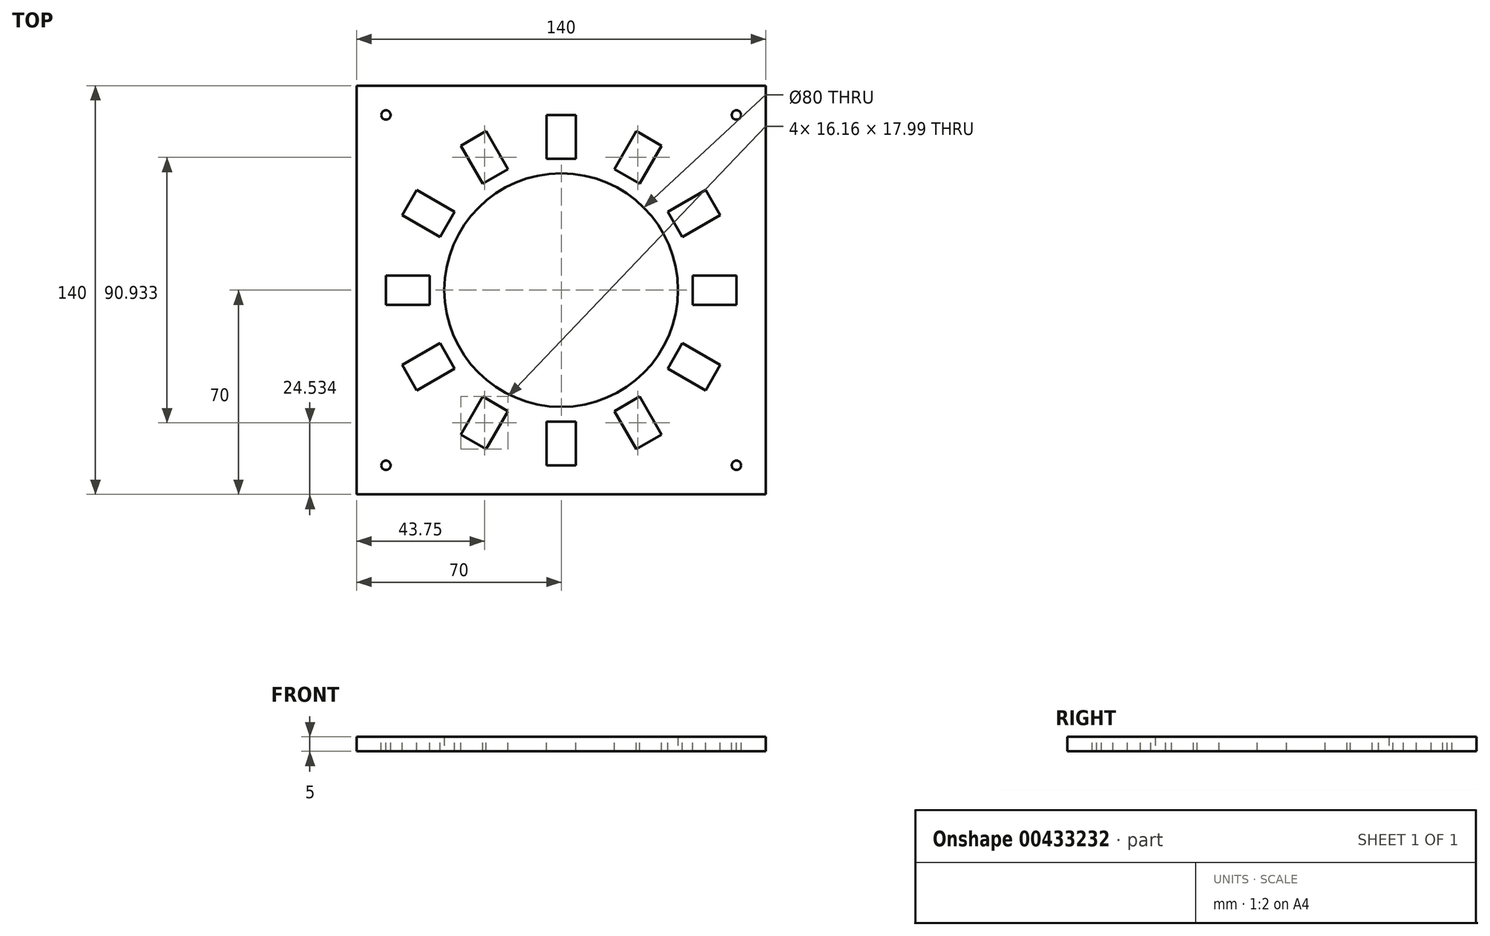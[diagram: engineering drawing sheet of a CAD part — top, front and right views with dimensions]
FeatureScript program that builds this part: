
annotation { "Feature Type Name" : "Feature", "Feature Type Description" : "" }
export const myFeature = defineFeature(function(context is Context, id is Id, definition is map)
    precondition{}
    {
        {
            var Q0;
            Q0=qCreatedBy(makeId("Top.planeOp"),FACE);
            var sketch = newSketch(context, id + "F0", { "sketchPlane" : qUnion([Q0])});
            skLineSegment(sketch, "E0.bottom", {"start": v(-65, 65) * mm, "end": v(65, 65) * mm});
            skLineSegment(sketch, "E0.top", {"start": v(-65, -65) * mm, "end": v(65, -65) * mm});
            skLineSegment(sketch, "E0.left", {"start": v(-65, 65) * mm, "end": v(-65, -65) * mm});
            skLineSegment(sketch, "E0.right", {"start": v(65, 65) * mm, "end": v(65, -65) * mm});
            skPoint(sketch, "E0.middle", {"position": v(0, 0) * mm});
            skLineSegment(sketch, "E1.top", {"start": v(-65, -70) * mm, "end": v(65, -70) * mm});
            skLineSegment(sketch, "E1.left", {"start": v(-65, -65) * mm, "end": v(-65, -70) * mm});
            skLineSegment(sketch, "E1.right", {"start": v(65, -65) * mm, "end": v(65, -70) * mm});
            skLineSegment(sketch, "E2.top", {"start": v(-65, 70) * mm, "end": v(65, 70) * mm});
            skLineSegment(sketch, "E2.left", {"start": v(-65, 65) * mm, "end": v(-65, 70) * mm});
            skLineSegment(sketch, "E2.right", {"start": v(65, 65) * mm, "end": v(65, 70) * mm});
            skLineSegment(sketch, "E3.bottom", {"start": v(-65, 70) * mm, "end": v(-70, 70) * mm});
            skLineSegment(sketch, "E3.top", {"start": v(-65, -70) * mm, "end": v(-70, -70) * mm});
            skLineSegment(sketch, "E3.left", {"start": v(-65, 70) * mm, "end": v(-65, -70) * mm});
            skLineSegment(sketch, "E3.right", {"start": v(-70, 70) * mm, "end": v(-70, -70) * mm});
            skLineSegment(sketch, "E4.bottom", {"start": v(65, 70) * mm, "end": v(70, 70) * mm});
            skLineSegment(sketch, "E4.top", {"start": v(65, -70) * mm, "end": v(70, -70) * mm});
            skLineSegment(sketch, "E4.left", {"start": v(65, 70) * mm, "end": v(65, -70) * mm});
            skLineSegment(sketch, "E4.right", {"start": v(70, 70) * mm, "end": v(70, -70) * mm});
            skSolve(sketch);
        }
        {
            var Q0;
            Q0 = qSketchRegion(id + "F0", true);
            extrude(context, id + "F1", {"entities" : qUnion([Q0]), "depth" : 70 * mm});
        }
        {
            var Q0;
            Q0=makeQuery(id+"F1.opExtrude","CAP_FACE",FACE,{"disambiguationData":[OSD([sQuery(id+"F0.wireOp",EDGE,"E0.top"),sQuery(id+"F0.wireOp",EDGE,"E1.top"),sQuery(id+"F0.wireOp",EDGE,"E0.bottom"),sQuery(id+"F0.wireOp",EDGE,"E2.top"),sQuery(id+"F0.wireOp",EDGE,"E3.bottom"),sQuery(id+"F0.wireOp",EDGE,"E3.top"),sQuery(id+"F0.wireOp",EDGE,"E3.left"),sQuery(id+"F0.wireOp",EDGE,"E3.right"),sQuery(id+"F0.wireOp",EDGE,"E4.bottom"),sQuery(id+"F0.wireOp",EDGE,"E4.top"),sQuery(id+"F0.wireOp",EDGE,"E4.left"),sQuery(id+"F0.wireOp",EDGE,"E4.right")])],"isStart":true});
            var sketch = newSketch(context, id + "F2", { "sketchPlane" : qUnion([Q0])});
            skLineSegment(sketch, "E5.bottom", {"start": v(-70, 70) * mm, "end": v(70, 70) * mm});
            skLineSegment(sketch, "E5.top", {"start": v(-70, -70) * mm, "end": v(70, -70) * mm});
            skLineSegment(sketch, "E5.left", {"start": v(-70, 70) * mm, "end": v(-70, -70) * mm});
            skLineSegment(sketch, "E5.right", {"start": v(70, 70) * mm, "end": v(70, -70) * mm});
            skSolve(sketch);
        }
        {
            var Q0;
            Q0 = qSketchRegion(id + "F2", true);
            extrude(context, id + "F3", {"entities" : qUnion([Q0]), "operationType" : NewBodyOperationType.ADD, "oppositeDirection" : true, "depth" : 5 * mm});
        }
        {
            var Q0;
            Q0=makeQuery(id+"F1.opExtrude","CAP_FACE",FACE,{"disambiguationData":[OSD([sQuery(id+"F0.wireOp",EDGE,"E0.top"),sQuery(id+"F0.wireOp",EDGE,"E1.top"),sQuery(id+"F0.wireOp",EDGE,"E0.bottom"),sQuery(id+"F0.wireOp",EDGE,"E2.top"),sQuery(id+"F0.wireOp",EDGE,"E3.bottom"),sQuery(id+"F0.wireOp",EDGE,"E3.top"),sQuery(id+"F0.wireOp",EDGE,"E3.left"),sQuery(id+"F0.wireOp",EDGE,"E3.right"),sQuery(id+"F0.wireOp",EDGE,"E4.bottom"),sQuery(id+"F0.wireOp",EDGE,"E4.top"),sQuery(id+"F0.wireOp",EDGE,"E4.left"),sQuery(id+"F0.wireOp",EDGE,"E4.right")])],"isStart":false});
            var sketch = newSketch(context, id + "F4", { "sketchPlane" : qUnion([Q0])});
            skLineSegment(sketch, "E6.bottom", {"start": v(-70, 70) * mm, "end": v(70, 70) * mm});
            skLineSegment(sketch, "E6.top", {"start": v(-70, -70) * mm, "end": v(70, -70) * mm});
            skLineSegment(sketch, "E6.left", {"start": v(-70, 70) * mm, "end": v(-70, -70) * mm});
            skLineSegment(sketch, "E6.right", {"start": v(70, 70) * mm, "end": v(70, -70) * mm});
            skPoint(sketch, "E7.endSnap0", {"position": v(-65, 0) * mm});
            skCircle(sketch, "E8", {"center": v(0, 0) * mm, "radius": 40 * mm});
            skLineSegment(sketch, "E9", {"start": v(0, 0) * mm, "end": v(-40, 0) * mm, "construction": true});
            skSolve(sketch);
        }
        {
            var Q0;
            Q0 = qSketchRegion(id + "F4", true);
            extrude(context, id + "F5", {"entities" : qUnion([Q0]), "operationType" : NewBodyOperationType.ADD, "depth" : 5 * mm});
        }
        {
            var Q0;
            Q0=makeQuery(id+"F5.opExtrude","CAP_FACE",FACE,{"disambiguationData":[OSD([sQuery(id+"F4.wireOp",EDGE,"E6.bottom"),sQuery(id+"F4.wireOp",EDGE,"E6.top"),sQuery(id+"F4.wireOp",EDGE,"E6.left"),sQuery(id+"F4.wireOp",EDGE,"E6.right"),sQuery(id+"F4.wireOp",EDGE,"E8")])],"isStart":false});
            var sketch = newSketch(context, id + "F6", { "sketchPlane" : qUnion([Q0])});
            skLineSegment(sketch, "E10", {"start": v(-70, 0) * mm, "end": v(-65, 0) * mm, "construction": true});
            skPoint(sketch, "E10.endSnap0", {"position": v(-70, 0) * mm});
            skLineSegment(sketch, "E11", {"start": v(-65, 0) * mm, "end": v(0, 0) * mm, "construction": true});
            skSolve(sketch);
        }
        {
            var Q0;
            Q0=makeQuery(id+"F6.imprint","IMPRINT",FACE,{"disambiguationData":[TD([[makeQuery(id+"F6.imprint","IMPRINT",EDGE,{"derivedFrom":makeQuery(id+"F5.opExtrude","CAP_EDGE",EDGE,{"disambiguationData":[OSD([sQuery(id+"F4.wireOp",EDGE,"E6.bottom")])],"isStart":false})}),-1.0]])]});
            var sketch = newSketch(context, id + "F7", { "sketchPlane" : qUnion([Q0])});
            skLineSegment(sketch, "E12", {"start": v(0, 0) * mm, "end": v(-45, 0) * mm, "construction": true});
            skCircle(sketch, "E13", {"center": v(0, 0) * mm, "radius": 45 * mm, "construction": true});
            skLineSegment(sketch, "E14", {"start": v(0, 0) * mm, "end": v(-38.97, -22.5) * mm, "construction": true});
            skLineSegment(sketch, "E15.MirrorCS", {"start": v(0, 0) * mm, "end": v(-38.97, 22.5) * mm, "construction": true});
            skLineSegment(sketch, "E16.MirrorCS", {"start": v(0, 0) * mm, "end": v(-22.5, 38.97) * mm, "construction": true});
            skLineSegment(sketch, "E17.MirrorCS", {"start": v(0, 0) * mm, "end": v(0, 45) * mm, "construction": true});
            skLineSegment(sketch, "E18.MirrorCS", {"start": v(0, 0) * mm, "end": v(22.5, 38.97) * mm, "construction": true});
            skLineSegment(sketch, "E19.MirrorCS", {"start": v(0, 0) * mm, "end": v(38.97, 22.5) * mm, "construction": true});
            skLineSegment(sketch, "E20.MirrorCS", {"start": v(0, 0) * mm, "end": v(45, 0) * mm, "construction": true});
            skLineSegment(sketch, "E21.MirrorCS", {"start": v(0, 0) * mm, "end": v(38.97, -22.5) * mm, "construction": true});
            skLineSegment(sketch, "E22.MirrorCS", {"start": v(0, 0) * mm, "end": v(22.5, -38.97) * mm, "construction": true});
            skLineSegment(sketch, "E23.MirrorCS", {"start": v(0, 0) * mm, "end": v(0, -45) * mm, "construction": true});
            skLineSegment(sketch, "E24.MirrorCS", {"start": v(0, 0) * mm, "end": v(-22.5, -38.97) * mm, "construction": true});
            skLineSegment(sketch, "E25", {"start": v(-38.97, 22.5) * mm, "end": v(-51.96, 30) * mm});
            skLineSegment(sketch, "E26", {"start": v(-51.96, 30) * mm, "end": v(-49.46, 34.33) * mm});
            skLineSegment(sketch, "E27", {"start": v(-49.46, 34.33) * mm, "end": v(-36.47, 26.83) * mm});
            skLineSegment(sketch, "E28", {"start": v(-36.47, 26.83) * mm, "end": v(-38.97, 22.5) * mm});
            skLineSegment(sketch, "E29.MirrorCS", {"start": v(-51.96, 30) * mm, "end": v(-54.46, 25.67) * mm});
            skLineSegment(sketch, "E30.MirrorCS", {"start": v(-54.46, 25.67) * mm, "end": v(-41.47, 18.17) * mm});
            skLineSegment(sketch, "E31.MirrorCS", {"start": v(-41.47, 18.17) * mm, "end": v(-38.97, 22.5) * mm});
            skLineSegment(sketch, "E32.MirrorCS", {"start": v(-5, 60) * mm, "end": v(-5, 45) * mm});
            skLineSegment(sketch, "E33.MirrorCS", {"start": v(0, 60) * mm, "end": v(-5, 60) * mm});
            skLineSegment(sketch, "E34.MirrorCS", {"start": v(-5, 45) * mm, "end": v(0, 45) * mm});
            skLineSegment(sketch, "E35.MirrorCS", {"start": v(0, 45) * mm, "end": v(0, 60) * mm});
            skLineSegment(sketch, "E36.MirrorCS", {"start": v(5, 45) * mm, "end": v(0, 45) * mm});
            skLineSegment(sketch, "E37.MirrorCS", {"start": v(5, 60) * mm, "end": v(5, 45) * mm});
            skLineSegment(sketch, "E38.MirrorCS", {"start": v(0, 60) * mm, "end": v(5, 60) * mm});
            skLineSegment(sketch, "E39.MirrorCS", {"start": v(49.46, 34.33) * mm, "end": v(36.47, 26.83) * mm});
            skLineSegment(sketch, "E40.MirrorCS", {"start": v(51.96, 30) * mm, "end": v(49.46, 34.33) * mm});
            skLineSegment(sketch, "E41.MirrorCS", {"start": v(51.96, 30) * mm, "end": v(54.46, 25.67) * mm});
            skLineSegment(sketch, "E42.MirrorCS", {"start": v(54.46, 25.67) * mm, "end": v(41.47, 18.17) * mm});
            skLineSegment(sketch, "E43.MirrorCS", {"start": v(38.97, 22.5) * mm, "end": v(51.96, 30) * mm});
            skLineSegment(sketch, "E44.MirrorCS", {"start": v(36.47, 26.83) * mm, "end": v(38.97, 22.5) * mm});
            skLineSegment(sketch, "E45.MirrorCS", {"start": v(41.47, 18.17) * mm, "end": v(38.97, 22.5) * mm});
            skLineSegment(sketch, "E46", {"start": v(-38.97, 22.5) * mm, "end": v(-22.5, 38.97) * mm, "construction": true});
            skLineSegment(sketch, "E47", {"start": v(-30.74, 30.74) * mm, "end": v(0, 0) * mm, "construction": true});
            skLineSegment(sketch, "E48", {"start": v(-30.74, 30.74) * mm, "end": v(-31.82, 31.82) * mm, "construction": true});
            skLineSegment(sketch, "E49.MirrorCS", {"start": v(-22.5, 38.97) * mm, "end": v(-30, 51.96) * mm});
            skLineSegment(sketch, "E50.MirrorCS", {"start": v(-34.33, 49.46) * mm, "end": v(-26.83, 36.47) * mm});
            skLineSegment(sketch, "E51.MirrorCS", {"start": v(-30, 51.96) * mm, "end": v(-34.33, 49.46) * mm});
            skLineSegment(sketch, "E52.MirrorCS", {"start": v(-26.83, 36.47) * mm, "end": v(-22.5, 38.97) * mm});
            skLineSegment(sketch, "E53.MirrorCS", {"start": v(-18.17, 41.47) * mm, "end": v(-22.5, 38.97) * mm});
            skLineSegment(sketch, "E54.MirrorCS", {"start": v(-25.67, 54.46) * mm, "end": v(-18.17, 41.47) * mm});
            skLineSegment(sketch, "E55.MirrorCS", {"start": v(-30, 51.96) * mm, "end": v(-25.67, 54.46) * mm});
            skLineSegment(sketch, "E56.MirrorCS", {"start": v(54.46, -25.67) * mm, "end": v(41.47, -18.17) * mm});
            skLineSegment(sketch, "E57.MirrorCS", {"start": v(41.47, -18.17) * mm, "end": v(38.97, -22.5) * mm});
            skLineSegment(sketch, "E58.MirrorCS", {"start": v(51.96, -30) * mm, "end": v(54.46, -25.67) * mm});
            skLineSegment(sketch, "E59.MirrorCS", {"start": v(51.96, -30) * mm, "end": v(49.46, -34.33) * mm});
            skLineSegment(sketch, "E60.MirrorCS", {"start": v(38.97, -22.5) * mm, "end": v(51.96, -30) * mm});
            skLineSegment(sketch, "E61.MirrorCS", {"start": v(49.46, -34.33) * mm, "end": v(36.47, -26.83) * mm});
            skLineSegment(sketch, "E62.MirrorCS", {"start": v(36.47, -26.83) * mm, "end": v(38.97, -22.5) * mm});
            skLineSegment(sketch, "E63.MirrorCS", {"start": v(-5, -60) * mm, "end": v(-5, -45) * mm});
            skLineSegment(sketch, "E64.MirrorCS", {"start": v(0, -45) * mm, "end": v(0, -60) * mm});
            skLineSegment(sketch, "E65.MirrorCS", {"start": v(-5, -45) * mm, "end": v(0, -45) * mm});
            skLineSegment(sketch, "E66.MirrorCS", {"start": v(5, -45) * mm, "end": v(0, -45) * mm});
            skLineSegment(sketch, "E67.MirrorCS", {"start": v(5, -60) * mm, "end": v(5, -45) * mm});
            skLineSegment(sketch, "E68.MirrorCS", {"start": v(0, -60) * mm, "end": v(5, -60) * mm});
            skLineSegment(sketch, "E69.MirrorCS", {"start": v(0, -60) * mm, "end": v(-5, -60) * mm});
            skLineSegment(sketch, "E70.MirrorCS", {"start": v(-49.46, -34.33) * mm, "end": v(-36.47, -26.83) * mm});
            skLineSegment(sketch, "E71.MirrorCS", {"start": v(-54.46, -25.67) * mm, "end": v(-41.47, -18.17) * mm});
            skLineSegment(sketch, "E72.MirrorCS", {"start": v(-38.97, -22.5) * mm, "end": v(-51.96, -30) * mm});
            skLineSegment(sketch, "E73.MirrorCS", {"start": v(-51.96, -30) * mm, "end": v(-49.46, -34.33) * mm});
            skLineSegment(sketch, "E74.MirrorCS", {"start": v(-51.96, -30) * mm, "end": v(-54.46, -25.67) * mm});
            skLineSegment(sketch, "E75.MirrorCS", {"start": v(-36.47, -26.83) * mm, "end": v(-38.97, -22.5) * mm});
            skLineSegment(sketch, "E76.MirrorCS", {"start": v(-41.47, -18.17) * mm, "end": v(-38.97, -22.5) * mm});
            skLineSegment(sketch, "E77.MirrorCS", {"start": v(25.67, 54.46) * mm, "end": v(18.17, 41.47) * mm});
            skLineSegment(sketch, "E78.MirrorCS", {"start": v(22.5, 38.97) * mm, "end": v(30, 51.96) * mm});
            skLineSegment(sketch, "E79.MirrorCS", {"start": v(34.33, 49.46) * mm, "end": v(26.83, 36.47) * mm});
            skLineSegment(sketch, "E80.MirrorCS", {"start": v(30, 51.96) * mm, "end": v(34.33, 49.46) * mm});
            skLineSegment(sketch, "E81.MirrorCS", {"start": v(30, 51.96) * mm, "end": v(25.67, 54.46) * mm});
            skLineSegment(sketch, "E82.MirrorCS", {"start": v(18.17, 41.47) * mm, "end": v(22.5, 38.97) * mm});
            skLineSegment(sketch, "E83.MirrorCS", {"start": v(26.83, 36.47) * mm, "end": v(22.5, 38.97) * mm});
            skLineSegment(sketch, "E84.MirrorCS", {"start": v(45, 0) * mm, "end": v(60, 0) * mm});
            skLineSegment(sketch, "E85.MirrorCS", {"start": v(60, 5) * mm, "end": v(45, 5) * mm});
            skLineSegment(sketch, "E86.MirrorCS", {"start": v(45, 5) * mm, "end": v(45, 0) * mm});
            skLineSegment(sketch, "E87.MirrorCS", {"start": v(45, -5) * mm, "end": v(45, 0) * mm});
            skLineSegment(sketch, "E88.MirrorCS", {"start": v(60, -5) * mm, "end": v(45, -5) * mm});
            skLineSegment(sketch, "E89.MirrorCS", {"start": v(60, 0) * mm, "end": v(60, -5) * mm});
            skLineSegment(sketch, "E90.MirrorCS", {"start": v(60, 0) * mm, "end": v(60, 5) * mm});
            skLineSegment(sketch, "E91.MirrorCS", {"start": v(34.33, -49.46) * mm, "end": v(26.83, -36.47) * mm});
            skLineSegment(sketch, "E92.MirrorCS", {"start": v(26.83, -36.47) * mm, "end": v(22.5, -38.97) * mm});
            skLineSegment(sketch, "E93.MirrorCS", {"start": v(30, -51.96) * mm, "end": v(34.33, -49.46) * mm});
            skLineSegment(sketch, "E94.MirrorCS", {"start": v(22.5, -38.97) * mm, "end": v(30, -51.96) * mm});
            skLineSegment(sketch, "E95.MirrorCS", {"start": v(30, -51.96) * mm, "end": v(25.67, -54.46) * mm});
            skLineSegment(sketch, "E96.MirrorCS", {"start": v(25.67, -54.46) * mm, "end": v(18.17, -41.47) * mm});
            skLineSegment(sketch, "E97.MirrorCS", {"start": v(18.17, -41.47) * mm, "end": v(22.5, -38.97) * mm});
            skLineSegment(sketch, "E98.MirrorCS", {"start": v(-34.33, -49.46) * mm, "end": v(-26.83, -36.47) * mm});
            skLineSegment(sketch, "E99.MirrorCS", {"start": v(-22.5, -38.97) * mm, "end": v(-30, -51.96) * mm});
            skLineSegment(sketch, "E100.MirrorCS", {"start": v(-25.67, -54.46) * mm, "end": v(-18.17, -41.47) * mm});
            skLineSegment(sketch, "E101.MirrorCS", {"start": v(-30, -51.96) * mm, "end": v(-25.67, -54.46) * mm});
            skLineSegment(sketch, "E102.MirrorCS", {"start": v(-30, -51.96) * mm, "end": v(-34.33, -49.46) * mm});
            skLineSegment(sketch, "E103.MirrorCS", {"start": v(-26.83, -36.47) * mm, "end": v(-22.5, -38.97) * mm});
            skLineSegment(sketch, "E104.MirrorCS", {"start": v(-18.17, -41.47) * mm, "end": v(-22.5, -38.97) * mm});
            skLineSegment(sketch, "E105.MirrorCS", {"start": v(-60, 5) * mm, "end": v(-45, 5) * mm});
            skLineSegment(sketch, "E106.MirrorCS", {"start": v(-60, -5) * mm, "end": v(-45, -5) * mm});
            skLineSegment(sketch, "E107.MirrorCS", {"start": v(-45, 5) * mm, "end": v(-45, 0) * mm});
            skLineSegment(sketch, "E108.MirrorCS", {"start": v(-45, -5) * mm, "end": v(-45, 0) * mm});
            skLineSegment(sketch, "E109.MirrorCS", {"start": v(-45, 0) * mm, "end": v(-60, 0) * mm});
            skLineSegment(sketch, "E110.MirrorCS", {"start": v(-60, 0) * mm, "end": v(-60, 5) * mm});
            skLineSegment(sketch, "E111.MirrorCS", {"start": v(-60, 0) * mm, "end": v(-60, -5) * mm});
            skSolve(sketch);
        }
        {
            var Q0;
            Q0 = qSketchRegion(id + "F7", true);
            extrude(context, id + "F8", {"entities" : qUnion([Q0]), "operationType" : NewBodyOperationType.REMOVE, "endBound" : BoundingType.UP_TO_NEXT, "oppositeDirection" : true, "depth" : 25 * mm});
        }
        {
            var Q0;
            Q0=makeQuery(id+"F5.boolean.opBoolean","MERGE",FACE,{"derivedFrom":[makeQuery(id+"F1.opExtrude","SWEPT_FACE",FACE,{"disambiguationData":[OSD([sQuery(id+"F0.wireOp",EDGE,"E1.top"),sQuery(id+"F0.wireOp",EDGE,"E3.top"),sQuery(id+"F0.wireOp",EDGE,"E4.top")])]}),makeQuery(id+"F5.opExtrude","SWEPT_FACE",FACE,{"disambiguationData":[OSD([sQuery(id+"F4.wireOp",EDGE,"E6.top")])]})]});
            var sketch = newSketch(context, id + "F9", { "sketchPlane" : qUnion([Q0])});
            skLineSegment(sketch, "E112", {"start": v(-70, 75) * mm, "end": v(-70, 70) * mm, "construction": true});
            skLineSegment(sketch, "E113.bottom", {"start": v(-70, 70) * mm, "end": v(70, 70) * mm});
            skLineSegment(sketch, "E113.top", {"start": v(-70, 0) * mm, "end": v(70, 0) * mm});
            skLineSegment(sketch, "E113.left", {"start": v(-70, 70) * mm, "end": v(-70, 0) * mm});
            skLineSegment(sketch, "E113.right", {"start": v(70, 70) * mm, "end": v(70, 0) * mm});
            skSolve(sketch);
        }
        {
            var Q0;
            Q0 = qSketchRegion(id + "F9", true);
            var Q1;
            Q1=makeQuery(id+"F5.boolean.opBoolean","MERGE",FACE,{"derivedFrom":[makeQuery(id+"F1.opExtrude","SWEPT_FACE",FACE,{"disambiguationData":[OSD([sQuery(id+"F0.wireOp",EDGE,"E2.top"),sQuery(id+"F0.wireOp",EDGE,"E3.bottom"),sQuery(id+"F0.wireOp",EDGE,"E4.bottom")])]}),makeQuery(id+"F5.opExtrude","SWEPT_FACE",FACE,{"disambiguationData":[OSD([sQuery(id+"F4.wireOp",EDGE,"E6.bottom")])]})]});
            extrude(context, id + "F10", {"entities" : qUnion([Q0]), "operationType" : NewBodyOperationType.REMOVE, "endBound" : BoundingType.UP_TO_SURFACE, "oppositeDirection" : true, "endBoundEntityFace" : qUnion([Q1]), "depth" : 25 * mm});
        }
        {
            var Q0;
            Q0=makeQuery(id+"F6.imprint","IMPRINT",FACE,{"disambiguationData":[TD([[makeQuery(id+"F6.imprint","IMPRINT",EDGE,{"derivedFrom":makeQuery(id+"F5.opExtrude","CAP_EDGE",EDGE,{"disambiguationData":[OSD([sQuery(id+"F4.wireOp",EDGE,"E6.bottom")])],"isStart":false})}),-1.0]])]});
            var sketch = newSketch(context, id + "F11", { "sketchPlane" : qUnion([Q0])});
            skLineSegment(sketch, "E114.bottom", {"start": v(-65, 65) * mm, "end": v(65, 65) * mm, "construction": true});
            skLineSegment(sketch, "E114.top", {"start": v(-65, -65) * mm, "end": v(65, -65) * mm, "construction": true});
            skLineSegment(sketch, "E114.left", {"start": v(-65, 65) * mm, "end": v(-65, -65) * mm, "construction": true});
            skLineSegment(sketch, "E114.right", {"start": v(65, 65) * mm, "end": v(65, -65) * mm, "construction": true});
            skPoint(sketch, "E114.middle", {"position": v(0, 0) * mm});
            skLineSegment(sketch, "E115.bottom", {"start": v(-60, 60) * mm, "end": v(60, 60) * mm, "construction": true});
            skLineSegment(sketch, "E115.top", {"start": v(-60, -60) * mm, "end": v(60, -60) * mm, "construction": true});
            skLineSegment(sketch, "E115.left", {"start": v(-60, 60) * mm, "end": v(-60, -60) * mm, "construction": true});
            skLineSegment(sketch, "E115.right", {"start": v(60, 60) * mm, "end": v(60, -60) * mm, "construction": true});
            skCircle(sketch, "E116", {"center": v(-60, -60) * mm, "radius": 1.6 * mm});
            skCircle(sketch, "E117.MirrorC", {"center": v(-60, 60) * mm, "radius": 1.6 * mm});
            skCircle(sketch, "E118.MirrorC", {"center": v(60, -60) * mm, "radius": 1.6 * mm});
            skCircle(sketch, "E119.MirrorC", {"center": v(60, 60) * mm, "radius": 1.6 * mm});
            skLineSegment(sketch, "E120", {"start": v(-60, 60) * mm, "end": v(-60, 50) * mm, "construction": true});
            skLineSegment(sketch, "E121.left", {"start": v(-60, 50) * mm, "end": v(-60, 40) * mm});
            skSolve(sketch);
        }
        {
            var Q0;
            Q0 = qSketchRegion(id + "F11", true);
            var Q1;
            Q1=makeQuery(id+"F10.boolean.opBoolean","MERGE",FACE,{"derivedFrom":[makeQuery(id+"F5.opExtrude","CAP_FACE",FACE,{"disambiguationData":[OSD([sQuery(id+"F4.wireOp",EDGE,"E6.bottom"),sQuery(id+"F4.wireOp",EDGE,"E6.top"),sQuery(id+"F4.wireOp",EDGE,"E6.left"),sQuery(id+"F4.wireOp",EDGE,"E6.right"),sQuery(id+"F4.wireOp",EDGE,"E8")])],"isStart":true}),makeQuery(id+"F10.opExtrude","SWEPT_FACE",FACE,{"disambiguationData":[OSD([sQuery(id+"F9.wireOp",EDGE,"E113.bottom")])]})]});
            extrude(context, id + "F12", {"entities" : qUnion([Q0]), "operationType" : NewBodyOperationType.REMOVE, "endBound" : BoundingType.UP_TO_SURFACE, "oppositeDirection" : true, "endBoundEntityFace" : qUnion([Q1]), "depth" : 25 * mm});
        }
    });
